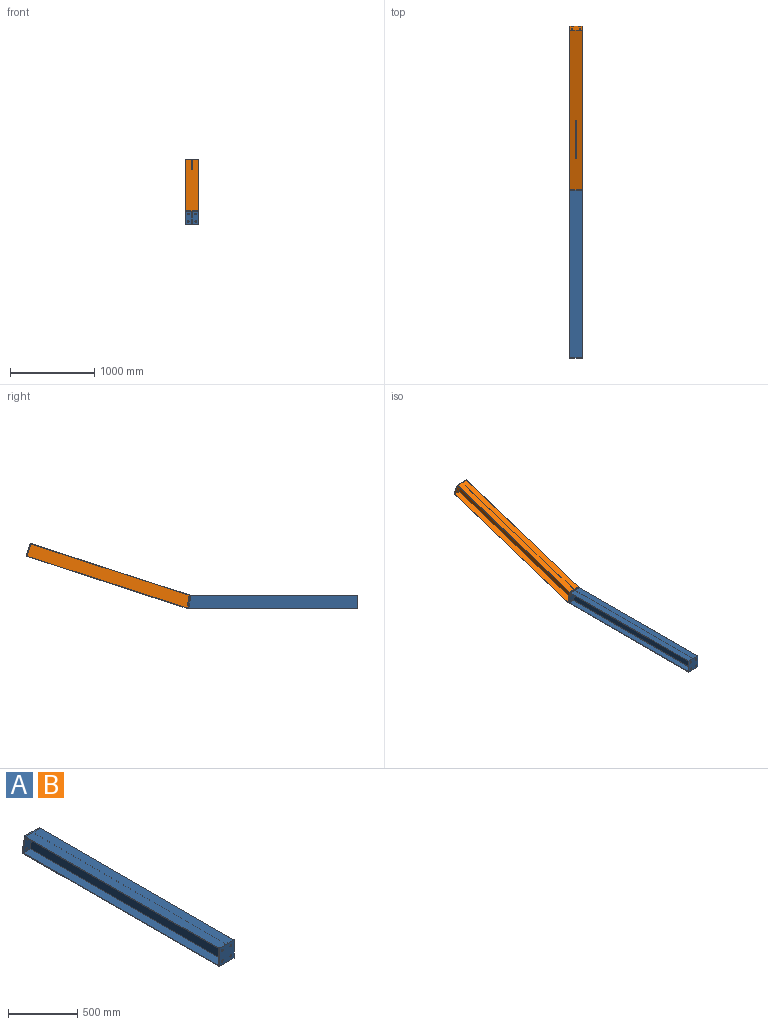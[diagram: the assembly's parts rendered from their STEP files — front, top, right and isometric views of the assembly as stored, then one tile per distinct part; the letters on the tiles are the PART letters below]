
ASSEMBLY  parts=2 mates=1
PART A: 26 faces, bbox 152x2014.8x161.6 mm
  f0: plane 1994.25x151mm, normal (1,0,0), area 299326.5mm2, adj f1,f9,f16,f17
  f1: plane 1970.34x73mm, normal (0,0,-1), area 143834.6mm2, adj f0,f8,f16,f17
  f2: plane 1979.62x152mm, normal (0,0,1), area 300902.8mm2, adj f6,f8,f15,f22
  f3: plane 1970.34x73mm, normal (0,0,-1), area 143834.6mm2, adj f4,f6,f10,f25
  f4: plane 1994.25x151mm, normal (-1,0,0), area 299326.5mm2, adj f3,f5,f10,f25
  f5: plane 1994.25x73mm, normal (0,0,1), area 145580.4mm2, adj f4,f6,f10,f25
  f6: plane 2014.84x161.56mm, normal (-1,0,0), area 21060.6mm2, adj f2,f3,f5,f7,f10,f15,f18,f22
  f7: plane 2004.97x152mm, normal (0,0,-1), area 304754.7mm2, adj f6,f8,f15,f18
  f8: plane 2014.84x161.56mm, normal (1,0,0), area 21060.6mm2, adj f1,f2,f7,f9,f15,f16,f17,f18
  f9: plane 1994.25x73mm, normal (0,0,1), area 145580.4mm2, adj f0,f8,f16,f17
  f10: plane 151x73mm, normal (0,1,0), area 10394.7mm2, adj f3,f4,f5,f6,f11,f14
  f11: cylinder r=10mm len=20mm, axis (0,1,0), area 628.3mm2, adj f10,f15
  f12: cylinder r=10mm len=20mm, axis (0,1,0), area 628.3mm2, adj f15,f16
  f13: cylinder r=10mm len=20mm, axis (0,1,0), area 628.3mm2, adj f15,f16
  f14: cylinder r=10mm len=20mm, axis (0,1,0), area 628.3mm2, adj f10,f15
  f15: plane 160x152mm, normal (0,-1,0), area 23063.4mm2, adj f2,f6,f7,f8,f11,f12,f13,f14
  f16: plane 151x73mm, normal (0,1,0), area 10394.7mm2, adj f0,f1,f8,f9,f12,f13
  f17: plane 151x73mm, normal (0,-0.99,-0.16), area 10532.1mm2, adj f0,f1,f8,f9,f19,f23
  f18: plane 152x9.88mm, normal (0,0.16,-0.99), area 1520mm2, adj f6,f7,f8,f24
  f19: cylinder r=10mm len=21.32mm, axis (0,-0.99,-0.16), area 628.3mm2, adj f17,f24
  f20: cylinder r=10mm len=21.32mm, axis (0,-0.99,-0.16), area 628.3mm2, adj f24,f25
  f21: cylinder r=10mm len=21.32mm, axis (0,-0.99,-0.16), area 628.3mm2, adj f24,f25
  f22: plane 152x9.88mm, normal (0,-0.16,0.99), area 1520mm2, adj f2,f6,f8,f24
  f23: cylinder r=10mm len=21.32mm, axis (0,-0.99,-0.16), area 628.3mm2, adj f17,f24
  f24: plane 160x152mm, normal (0,0.99,0.16), area 23366.5mm2, adj f6,f8,f18,f19,f20,f21,f22,f23
  f25: plane 151x73mm, normal (0,-0.99,-0.16), area 10532.1mm2, adj f3,f4,f5,f6,f20,f21
PART B: same geometry as A
PLACE A t=(-49.3,222.82,-377.72)mm
PLACE B rot(axis=(0,0.16,-0.99),180deg) t=(-49.3,208.03,-380.06)mm
MATE parallel B.f24 <-> A.f24  axis (0,-0.99,-0.16) through (-49.3,214.97,-376.01)mm
